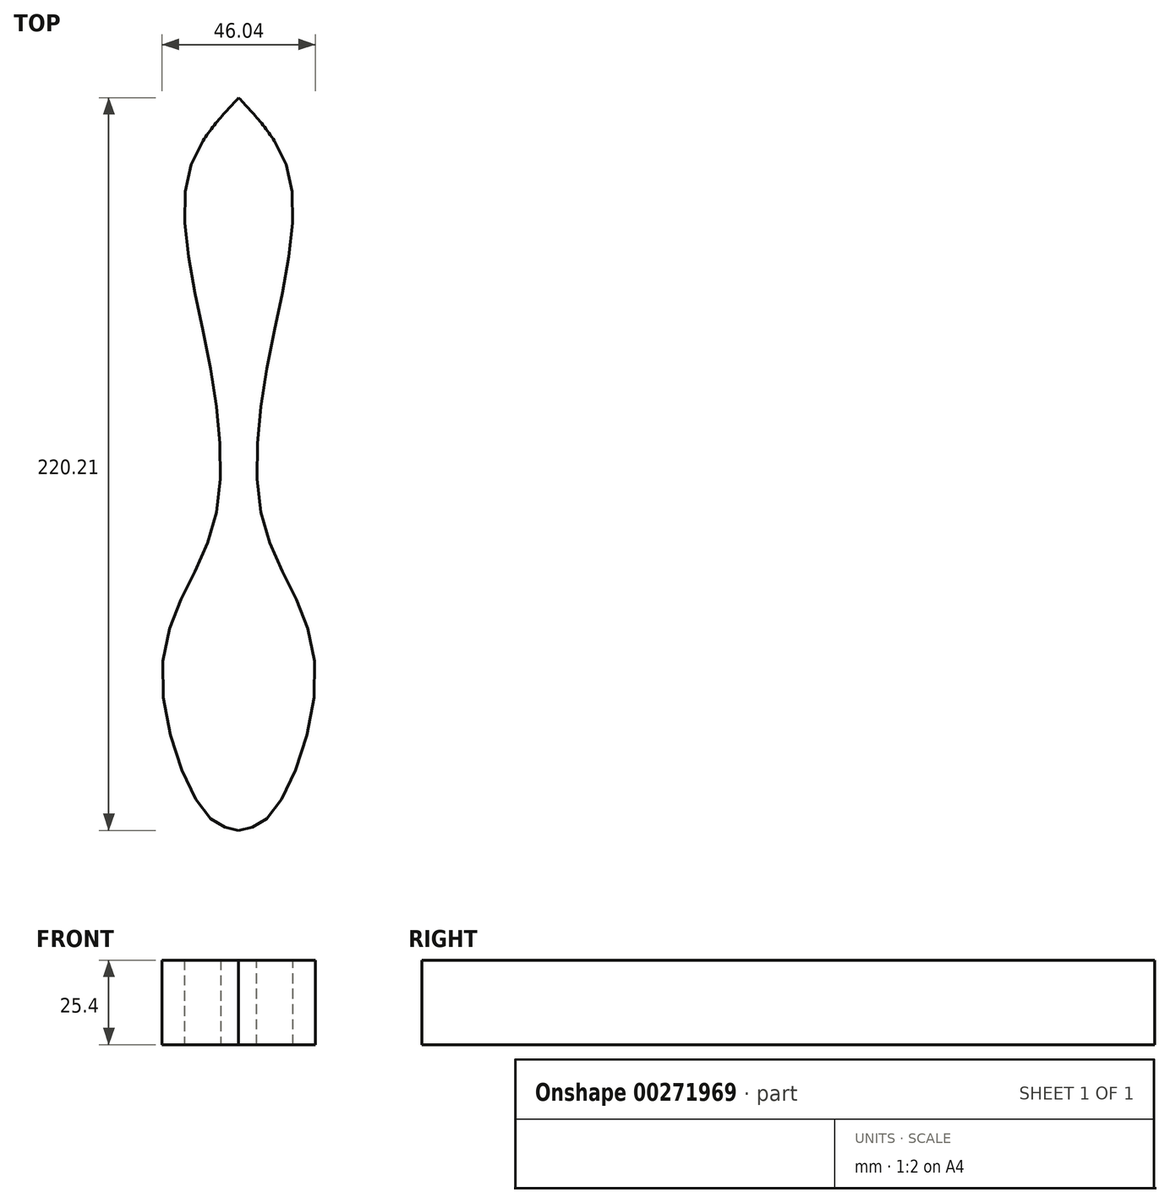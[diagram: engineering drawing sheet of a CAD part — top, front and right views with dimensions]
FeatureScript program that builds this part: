
annotation { "Feature Type Name" : "Feature", "Feature Type Description" : "" }
export const myFeature = defineFeature(function(context is Context, id is Id, definition is map)
    precondition{}
    {
        {
            var Q0;
            Q0=qCreatedBy(makeId("Right.planeOp"),FACE);
            var sketch = newSketch(context, id + "F0", { "sketchPlane" : qUnion([Q0])});
            skLineSegment(sketch, "E0.bottom", {"start": v(-69.72, 10.53) * mm, "end": v(159.32, 10.53) * mm});
            skLineSegment(sketch, "E0.top", {"start": v(-69.72, -15.02) * mm, "end": v(159.32, -15.02) * mm});
            skLineSegment(sketch, "E0.left", {"start": v(-69.72, 10.53) * mm, "end": v(-69.72, -15.02) * mm});
            skLineSegment(sketch, "E0.right", {"start": v(159.32, 10.53) * mm, "end": v(159.32, -15.02) * mm});
            skSolve(sketch);
        }
        {
            var Q0;
            Q0 = qSketchRegion(id + "F0", true);
            extrude(context, id + "F1", {"entities" : qUnion([Q0]), "endBound" : BoundingType.SYMMETRIC, "depth" : 50.8 * mm});
        }
        {
            var Q0;
            Q0=makeQuery(id+"F1.opExtrude","SWEPT_FACE",FACE,{"disambiguationData":[OSD([sQuery(id+"F0.wireOp",EDGE,"E0.bottom")])]});
            var sketch = newSketch(context, id + "F2", { "sketchPlane" : qUnion([Q0])});
            skFitSpline(sketch, "E1", {"points": [v(0, 150.5) * mm, v(15.5, 126.1) * mm, v(9.63, 74.95) * mm, v(7.86, 20.87) * mm, v(22.85, -19.1) * mm, v(9.33, -65.26) * mm, v(0, -69.72) * mm], "startDerivative": vector(135.96, -145.76) * mm, "endDerivative": vector(-103.88, -15.68) * mm});
            skFitSpline(sketch, "E2.MirrorCS", {"points": [v(0, 150.5) * mm, v(-15.5, 126.1) * mm, v(-9.63, 74.95) * mm, v(-7.86, 20.87) * mm, v(-22.85, -19.1) * mm, v(-9.33, -65.26) * mm, v(0, -69.72) * mm], "startDerivative": vector(-135.96, -145.76) * mm, "endDerivative": vector(103.88, -15.68) * mm});
            skArc(sketch, "E3.filletArc", {"start": v(10.74, 137.45) * mm, "mid": v(0, 143.37) * mm, "end": v(-10.74, 137.45) * mm});
            skSolve(sketch);
        }
        {
            var Q0;
            Q0=makeQuery(id+"F2.imprint","IMPRINT",FACE,{"disambiguationData":[TD([[makeQuery(id+"F2.imprint","IMPRINT",EDGE,{"derivedFrom":sQuery(id+"F2.wireOp",EDGE,"E1")}),-1.0]])]});
            extrude(context, id + "F3", {"entities" : qUnion([Q0]), "operationType" : NewBodyOperationType.INTERSECT, "oppositeDirection" : true, "depth" : 25.4 * mm});
        }
    });
